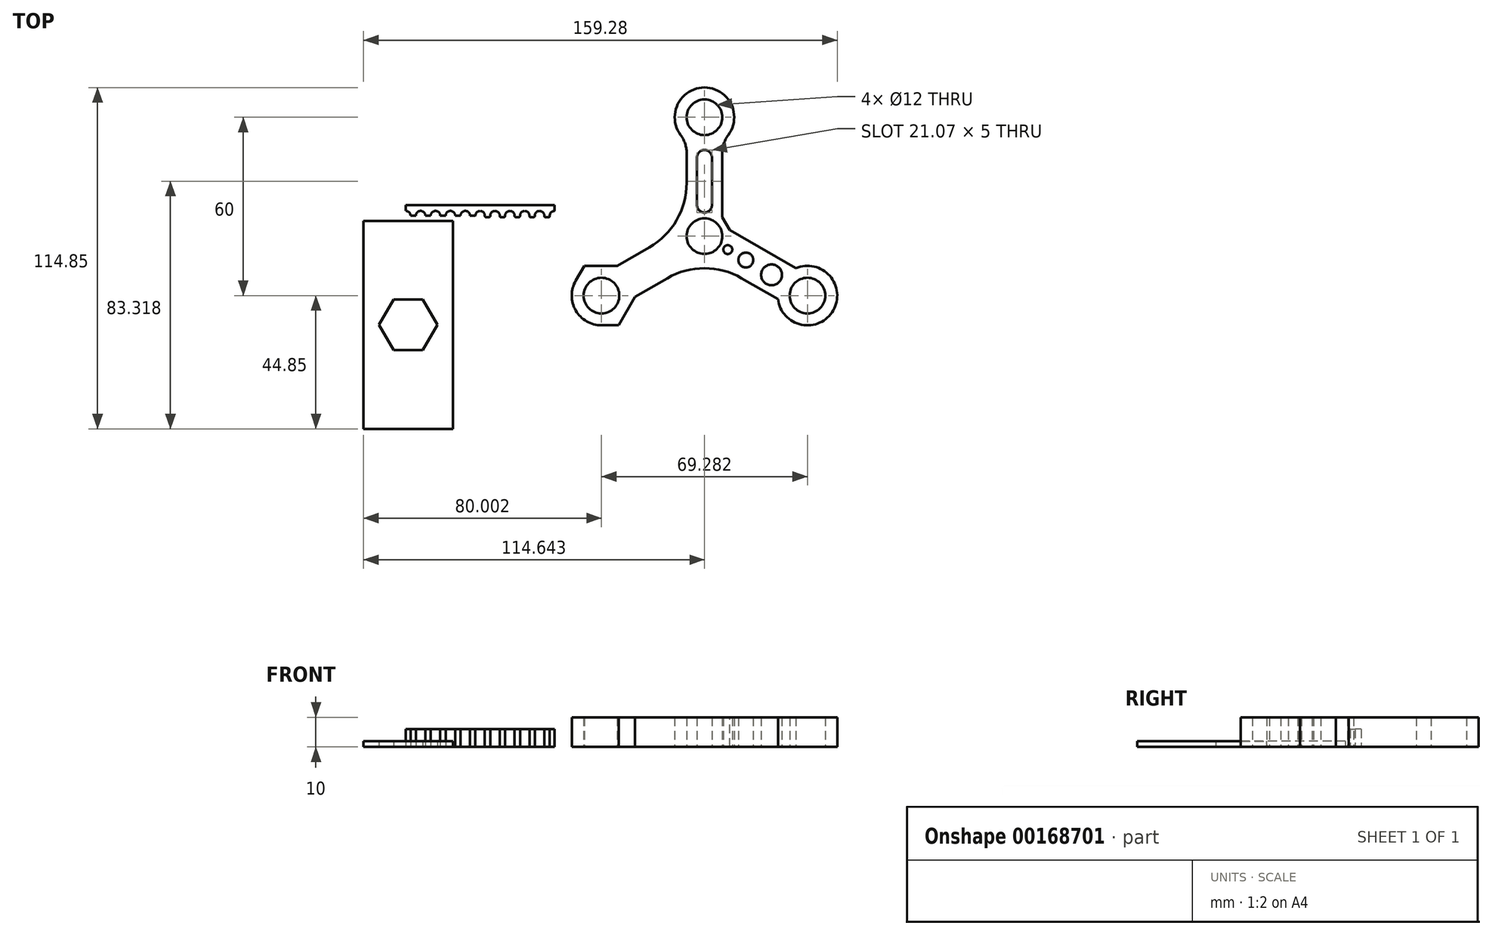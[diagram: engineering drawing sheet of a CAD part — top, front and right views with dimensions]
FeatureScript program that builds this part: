
annotation { "Feature Type Name" : "Feature", "Feature Type Description" : "" }
export const myFeature = defineFeature(function(context is Context, id is Id, definition is map)
    precondition{}
    {
        {
            var Q0;
            Q0=qCreatedBy(makeId("Top.planeOp"),FACE);
            var sketch = newSketch(context, id + "F0", { "sketchPlane" : qUnion([Q0])});
            skLineSegment(sketch, "E0", {"start": v(-55.05, 8.38) * mm, "end": v(-5.05, 8.38) * mm, "construction": true});
            skLineSegment(sketch, "E1.0", {"start": v(-55.05, 6.89) * mm, "end": v(-5.05, 6.89) * mm, "construction": true});
            skLineSegment(sketch, "E2.0", {"start": v(-55.05, 4.58) * mm, "end": v(-5.05, 4.58) * mm});
            skLineSegment(sketch, "E3", {"start": v(-36.36, 4.58) * mm, "end": v(-36.36, 8.38) * mm, "construction": true});
            skArc(sketch, "E4", {"start": v(-37.95, 6.89) * mm, "mid": v(-36.36, 8.48) * mm, "end": v(-34.77, 6.89) * mm});
            skLineSegment(sketch, "E5.0", {"start": v(-55.05, 6.32) * mm, "end": v(-5.05, 6.32) * mm, "construction": true});
            skLineSegment(sketch, "E6", {"start": v(-34.27, 6.32) * mm, "end": v(-32.77, 6.32) * mm});
            skLineSegment(sketch, "E7", {"start": v(-34.77, 6.89) * mm, "end": v(-34.77, 6.82) * mm});
            skLineSegment(sketch, "E8", {"start": v(-37.95, 6.89) * mm, "end": v(-37.95, 6.82) * mm});
            skLineSegment(sketch, "E9", {"start": v(-38.45, 6.32) * mm, "end": v(-38.95, 6.32) * mm});
            skPoint(sketch, "E10.visualSharp", {"position": v(-37.95, 6.32) * mm});
            skArc(sketch, "E10.filletArc", {"start": v(-38.45, 6.32) * mm, "mid": v(-38.1, 6.46) * mm, "end": v(-37.95, 6.82) * mm});
            skPoint(sketch, "E11.visualSharp", {"position": v(-34.77, 6.32) * mm});
            skArc(sketch, "E11.filletArc", {"start": v(-34.77, 6.82) * mm, "mid": v(-34.63, 6.46) * mm, "end": v(-34.27, 6.32) * mm});
            skLineSegment(sketch, "E12.1.0.0", {"start": v(-33.45, 6.32) * mm, "end": v(-33.95, 6.32) * mm});
            skArc(sketch, "E12.1.0.1", {"start": v(-33.45, 6.32) * mm, "mid": v(-33.1, 6.46) * mm, "end": v(-32.95, 6.82) * mm});
            skLineSegment(sketch, "E12.1.0.2", {"start": v(-32.95, 6.89) * mm, "end": v(-32.95, 6.82) * mm});
            skArc(sketch, "E12.1.0.3", {"start": v(-32.95, 6.89) * mm, "mid": v(-31.36, 8.48) * mm, "end": v(-29.77, 6.89) * mm});
            skLineSegment(sketch, "E12.1.0.4", {"start": v(-29.77, 6.89) * mm, "end": v(-29.77, 6.82) * mm});
            skArc(sketch, "E12.1.0.5", {"start": v(-29.77, 6.82) * mm, "mid": v(-29.63, 6.46) * mm, "end": v(-29.27, 6.32) * mm});
            skLineSegment(sketch, "E12.1.0.6", {"start": v(-29.27, 6.32) * mm, "end": v(-27.77, 6.32) * mm});
            skLineSegment(sketch, "E12.2.0.0", {"start": v(-28.45, 6.32) * mm, "end": v(-28.95, 6.32) * mm});
            skArc(sketch, "E12.2.0.1", {"start": v(-28.45, 6.32) * mm, "mid": v(-28.1, 6.46) * mm, "end": v(-27.95, 6.82) * mm});
            skLineSegment(sketch, "E12.2.0.2", {"start": v(-27.95, 6.89) * mm, "end": v(-27.95, 6.82) * mm});
            skArc(sketch, "E12.2.0.3", {"start": v(-27.95, 6.89) * mm, "mid": v(-26.36, 8.48) * mm, "end": v(-24.77, 6.89) * mm});
            skLineSegment(sketch, "E12.2.0.4", {"start": v(-24.77, 6.89) * mm, "end": v(-24.77, 6.82) * mm});
            skArc(sketch, "E12.2.0.5", {"start": v(-24.77, 6.82) * mm, "mid": v(-24.63, 6.46) * mm, "end": v(-24.27, 6.32) * mm});
            skLineSegment(sketch, "E12.2.0.6", {"start": v(-24.27, 6.32) * mm, "end": v(-22.77, 6.32) * mm});
            skLineSegment(sketch, "E12.3.0.0", {"start": v(-23.45, 6.32) * mm, "end": v(-23.95, 6.32) * mm});
            skArc(sketch, "E12.3.0.1", {"start": v(-23.45, 6.32) * mm, "mid": v(-23.1, 6.46) * mm, "end": v(-22.95, 6.82) * mm});
            skLineSegment(sketch, "E12.3.0.2", {"start": v(-22.95, 6.89) * mm, "end": v(-22.95, 6.82) * mm});
            skArc(sketch, "E12.3.0.3", {"start": v(-22.95, 6.89) * mm, "mid": v(-21.36, 8.48) * mm, "end": v(-19.77, 6.89) * mm});
            skLineSegment(sketch, "E12.3.0.4", {"start": v(-19.77, 6.89) * mm, "end": v(-19.77, 6.82) * mm});
            skArc(sketch, "E12.3.0.5", {"start": v(-19.77, 6.82) * mm, "mid": v(-19.63, 6.46) * mm, "end": v(-19.27, 6.32) * mm});
            skLineSegment(sketch, "E12.3.0.6", {"start": v(-19.27, 6.32) * mm, "end": v(-17.77, 6.32) * mm});
            skLineSegment(sketch, "E12.4.0.0", {"start": v(-18.45, 6.32) * mm, "end": v(-18.95, 6.32) * mm});
            skArc(sketch, "E12.4.0.1", {"start": v(-18.45, 6.32) * mm, "mid": v(-18.1, 6.46) * mm, "end": v(-17.95, 6.82) * mm});
            skLineSegment(sketch, "E12.4.0.2", {"start": v(-17.95, 6.89) * mm, "end": v(-17.95, 6.82) * mm});
            skArc(sketch, "E12.4.0.3", {"start": v(-17.95, 6.89) * mm, "mid": v(-16.36, 8.48) * mm, "end": v(-14.77, 6.89) * mm});
            skLineSegment(sketch, "E12.4.0.4", {"start": v(-14.77, 6.89) * mm, "end": v(-14.77, 6.82) * mm});
            skArc(sketch, "E12.4.0.5", {"start": v(-14.77, 6.82) * mm, "mid": v(-14.63, 6.46) * mm, "end": v(-14.27, 6.32) * mm});
            skLineSegment(sketch, "E12.4.0.6", {"start": v(-14.27, 6.32) * mm, "end": v(-12.77, 6.32) * mm});
            skLineSegment(sketch, "E12.direction1", {"start": v(-38.95, 6.32) * mm, "end": v(-33.95, 6.32) * mm, "construction": true});
            skLineSegment(sketch, "E13.0.5.0", {"start": v(-13.45, 6.32) * mm, "end": v(-13.95, 6.32) * mm});
            skArc(sketch, "E13.3.5.0", {"start": v(-13.45, 6.32) * mm, "mid": v(-13.1, 6.46) * mm, "end": v(-12.95, 6.82) * mm});
            skLineSegment(sketch, "E13.7.5.0", {"start": v(-12.95, 6.89) * mm, "end": v(-12.95, 6.82) * mm});
            skArc(sketch, "E13.10.5.0", {"start": v(-12.95, 6.89) * mm, "mid": v(-11.36, 8.48) * mm, "end": v(-9.77, 6.89) * mm});
            skLineSegment(sketch, "E13.14.5.0", {"start": v(-9.77, 6.89) * mm, "end": v(-9.77, 6.82) * mm});
            skArc(sketch, "E13.17.5.0", {"start": v(-9.77, 6.82) * mm, "mid": v(-9.63, 6.46) * mm, "end": v(-9.27, 6.32) * mm});
            skLineSegment(sketch, "E13.21.5.0", {"start": v(-9.27, 6.32) * mm, "end": v(-7.77, 6.32) * mm});
            skLineSegment(sketch, "E14", {"start": v(-36.36, 8.48) * mm, "end": v(-36.36, 10.48) * mm});
            skPoint(sketch, "E14.endSnap0", {"position": v(-36.36, 8.48) * mm});
            skLineSegment(sketch, "E15", {"start": v(-36.36, 10.48) * mm, "end": v(-11.36, 10.48) * mm});
            skLineSegment(sketch, "E16", {"start": v(-11.36, 10.48) * mm, "end": v(-11.36, 8.48) * mm});
            skCircle(sketch, "E17", {"center": v(-41.36, 6.89) * mm, "radius": 1.6 * mm});
            skCircle(sketch, "E18.1.0.0", {"center": v(-46.36, 6.89) * mm, "radius": 1.6 * mm});
            skCircle(sketch, "E18.2.0.0", {"center": v(-51.36, 6.89) * mm, "radius": 1.6 * mm});
            skCircle(sketch, "E18.3.0.0", {"center": v(-56.36, 6.89) * mm, "radius": 1.6 * mm});
            skCircle(sketch, "E18.4.0.0", {"center": v(-61.36, 6.89) * mm, "radius": 1.6 * mm});
            skCircle(sketch, "E18.5.0.0", {"center": v(-66.36, 6.89) * mm, "radius": 1.6 * mm});
            skLineSegment(sketch, "E18.direction1", {"start": v(-41.36, 6.89) * mm, "end": v(-46.36, 6.89) * mm, "construction": true});
            skLineSegment(sketch, "E19", {"start": v(-39.76, 6.89) * mm, "end": v(-37.95, 6.89) * mm});
            skLineSegment(sketch, "E20", {"start": v(-36.36, 10.48) * mm, "end": v(-61.36, 10.48) * mm});
            skLineSegment(sketch, "E21", {"start": v(-61.36, 10.48) * mm, "end": v(-61.36, 8.49) * mm});
            skLineSegment(sketch, "E22", {"start": v(-59.76, 6.89) * mm, "end": v(-57.96, 6.89) * mm});
            skLineSegment(sketch, "E23", {"start": v(-54.76, 6.89) * mm, "end": v(-52.96, 6.89) * mm});
            skLineSegment(sketch, "E24", {"start": v(-49.76, 6.89) * mm, "end": v(-47.96, 6.89) * mm});
            skLineSegment(sketch, "E25", {"start": v(-44.76, 6.89) * mm, "end": v(-42.96, 6.89) * mm});
            skSolve(sketch);
        }
        {
            var Q0;
            {var subQ5=sQuery(id+"F0.wireOp",EDGE,"E14");Q0=makeQuery(id+"F0.imprint","IMPRINT",FACE,{"disambiguationData":[TD([[makeQuery(id+"F0.imprint","IMPRINT",EDGE,{"derivedFrom":subQ5}),1.0]])]});}
            var Q1;
            {var subQ7=sQuery(id+"F0.wireOp",EDGE,"E7");Q1=makeQuery(id+"F0.imprint","IMPRINT",FACE,{"disambiguationData":[TD([[makeQuery(id+"F0.imprint","IMPRINT",EDGE,{"derivedFrom":subQ7}),1.0]])]});}
            extrude(context, id + "F1", {"entities" : qUnion([Q0, Q1]), "depth" : 6 * mm});
        }
        {
            var Q0;
            Q0=qCreatedBy(makeId("Top.planeOp"),FACE);
            var sketch = newSketch(context, id + "F2", { "sketchPlane" : qUnion([Q0])});
            skCircle(sketch, "E26", {"center": v(39.08, 0) * mm, "radius": 6 * mm});
            skLineSegment(sketch, "E27", {"start": v(33.08, 0) * mm, "end": v(45.08, 0) * mm, "construction": true});
            skLineSegment(sketch, "E28.bottom", {"start": v(33.08, 0) * mm, "end": v(45.08, 0) * mm});
            skLineSegment(sketch, "E28.top", {"start": v(33.08, 40) * mm, "end": v(45.08, 40) * mm});
            skLineSegment(sketch, "E28.left", {"start": v(33.08, 0) * mm, "end": v(33.08, 28) * mm});
            skLineSegment(sketch, "E28.right", {"start": v(45.08, 0) * mm, "end": v(45.08, 28) * mm});
            skCircle(sketch, "E29", {"center": v(39.08, 40) * mm, "radius": 6 * mm});
            skLineSegment(sketch, "E30.1.0", {"start": v(36.08, 5.2) * mm, "end": v(1.44, -14.8) * mm});
            skCircle(sketch, "E30.1.1", {"center": v(4.44, -20) * mm, "radius": 10 * mm});
            skCircle(sketch, "E30.1.2", {"center": v(4.44, -20) * mm, "radius": 6 * mm});
            skLineSegment(sketch, "E30.1.3", {"start": v(42.08, -5.2) * mm, "end": v(7.44, -25.2) * mm});
            skLineSegment(sketch, "E30.2.0", {"start": v(36.08, -5.2) * mm, "end": v(70.72, -25.2) * mm});
            skCircle(sketch, "E30.2.1", {"center": v(73.72, -20) * mm, "radius": 10 * mm});
            skCircle(sketch, "E30.2.2", {"center": v(73.72, -20) * mm, "radius": 6 * mm});
            skLineSegment(sketch, "E30.2.3", {"start": v(42.08, 5.2) * mm, "end": v(76.72, -14.8) * mm});
            skLineSegment(sketch, "E31", {"start": v(39.08, 10.43) * mm, "end": v(39.08, 26.5) * mm});
            skArc(sketch, "E32.0.startCap", {"start": v(41.58, 10.43) * mm, "mid": v(39.08, 7.93) * mm, "end": v(36.58, 10.43) * mm});
            skArc(sketch, "E32.0.endCap", {"start": v(36.58, 26.5) * mm, "mid": v(39.08, 29) * mm, "end": v(41.58, 26.5) * mm});
            skLineSegment(sketch, "E32.0.left", {"start": v(36.58, 10.43) * mm, "end": v(36.58, 26.5) * mm});
            skLineSegment(sketch, "E32.0.right", {"start": v(41.58, 10.43) * mm, "end": v(41.58, 26.5) * mm});
            skCircle(sketch, "E33.cCircle", {"center": v(4.44, -20) * mm, "radius": 10 * mm, "construction": true});
            skLineSegment(sketch, "E33.0", {"start": v(-1.33, -10) * mm, "end": v(10.22, -10) * mm});
            skLineSegment(sketch, "E33.1", {"start": v(10.22, -10) * mm, "end": v(15.99, -20) * mm});
            skLineSegment(sketch, "E33.2", {"start": v(15.99, -20) * mm, "end": v(10.22, -30) * mm});
            skLineSegment(sketch, "E33.3", {"start": v(10.22, -30) * mm, "end": v(-1.33, -30) * mm});
            skLineSegment(sketch, "E33.4", {"start": v(-1.33, -30) * mm, "end": v(-7.1, -20) * mm});
            skLineSegment(sketch, "E33.5", {"start": v(-7.1, -20) * mm, "end": v(-1.33, -10) * mm});
            skPoint(sketch, "E33.0.midPoint", {"position": v(4.44, -10) * mm});
            skLineSegment(sketch, "E34.bottom", {"start": v(-75.56, 5.15) * mm, "end": v(-45.56, 5.15) * mm});
            skLineSegment(sketch, "E34.top", {"start": v(-75.56, -64.85) * mm, "end": v(-45.56, -64.85) * mm});
            skLineSegment(sketch, "E34.left", {"start": v(-75.56, 5.15) * mm, "end": v(-75.56, -64.85) * mm});
            skLineSegment(sketch, "E34.right", {"start": v(-45.56, 5.15) * mm, "end": v(-45.56, -64.85) * mm});
            skCircle(sketch, "E35.cCircle", {"center": v(-60.56, -29.85) * mm, "radius": 8.5 * mm, "construction": true});
            skPoint(sketch, "E35.cCircle.centerSnap0", {"position": v(-60.56, -64.85) * mm});
            skPoint(sketch, "E35.cCircle.centerSnap1", {"position": v(-75.56, -29.85) * mm});
            skLineSegment(sketch, "E35.0", {"start": v(-65.46, -21.35) * mm, "end": v(-55.65, -21.35) * mm});
            skLineSegment(sketch, "E35.1", {"start": v(-55.65, -21.35) * mm, "end": v(-50.74, -29.85) * mm});
            skLineSegment(sketch, "E35.2", {"start": v(-50.74, -29.85) * mm, "end": v(-55.65, -38.35) * mm});
            skLineSegment(sketch, "E35.3", {"start": v(-55.65, -38.35) * mm, "end": v(-65.46, -38.35) * mm});
            skLineSegment(sketch, "E35.4", {"start": v(-65.46, -38.35) * mm, "end": v(-70.37, -29.85) * mm});
            skLineSegment(sketch, "E35.5", {"start": v(-70.37, -29.85) * mm, "end": v(-65.46, -21.35) * mm});
            skPoint(sketch, "E35.0.midPoint", {"position": v(-60.56, -21.35) * mm});
            skLineSegment(sketch, "E36", {"start": v(39.08, 0) * mm, "end": v(73.72, -20) * mm, "construction": true});
            skCircle(sketch, "E37", {"center": v(46.93, -4.53) * mm, "radius": 1.5 * mm});
            skCircle(sketch, "E38", {"center": v(53, -8.03) * mm, "radius": 2.5 * mm});
            skCircle(sketch, "E39", {"center": v(61.65, -13.03) * mm, "radius": 3.5 * mm});
            skArc(sketch, "E40", {"start": v(33.08, 32) * mm, "mid": v(39.08, 30) * mm, "end": v(45.08, 32) * mm});
            skArc(sketch, "E41", {"start": v(47.08, 34) * mm, "mid": v(39.08, 50) * mm, "end": v(31.08, 34) * mm});
            skPoint(sketch, "E42.newPointB", {"position": v(33.08, 40) * mm});
            skArc(sketch, "E42.filletArc", {"start": v(33.08, 28) * mm, "mid": v(32.57, 31.16) * mm, "end": v(31.08, 34) * mm});
            skPoint(sketch, "E43.newPointB", {"position": v(45.08, 40) * mm});
            skArc(sketch, "E43.filletArc", {"start": v(47.08, 34) * mm, "mid": v(45.6, 31.16) * mm, "end": v(45.08, 28) * mm});
            skSolve(sketch);
        }
        {
            var Q0;
            {var subQ1=sQuery(id+"F2.wireOp",EDGE,"E28.left");var subQ4=sQuery(id+"F2.wireOp",EDGE,"c7i8PMyH-ycge-szl3-A97O-6cANzthIr7NN");var subQ5=makeQuery(id+"F2.imprint","INTERSECT",VERTEX,{"derivedFrom":[subQ1,subQ4]});Q0=makeQuery(id+"F2.imprint","IMPRINT",FACE,{"disambiguationData":[TD([[makeQuery(id+"F2.imprint","IMPRINT",EDGE,{"disambiguationData":[TD([[subQ5,1.0]])],"derivedFrom":subQ4}),1.0]])]});}
            var Q1;
            {var subQ1=sQuery(id+"F2.wireOp",EDGE,"E28.left");var subQ4=sQuery(id+"F2.wireOp",EDGE,"c7i8PMyH-ycge-szl3-A97O-6cANzthIr7NN");var subQ5=makeQuery(id+"F2.imprint","INTERSECT",VERTEX,{"derivedFrom":[subQ1,subQ4]});Q1=makeQuery(id+"F2.imprint","IMPRINT",FACE,{"disambiguationData":[TD([[makeQuery(id+"F2.imprint","IMPRINT",EDGE,{"disambiguationData":[TD([[subQ5,-1.0]])],"derivedFrom":subQ4}),1.0]])]});}
            var Q2;
            {var subQ5=sQuery(id+"F2.wireOp",EDGE,"E30.1.0");var subQ6=sQuery(id+"F2.wireOp",EDGE,"E26");var subQ7=makeQuery(id+"F2.imprint","INTERSECT",VERTEX,{"derivedFrom":[subQ6,subQ5]});Q2=makeQuery(id+"F2.imprint","IMPRINT",FACE,{"disambiguationData":[TD([[makeQuery(id+"F2.imprint","IMPRINT",EDGE,{"disambiguationData":[TD([[subQ7,1.0]])],"derivedFrom":subQ6}),-1.0]])]});}
            var Q3;
            {var subQ1=sQuery(id+"F2.wireOp",EDGE,"E30.1.0");var subQ5=sQuery(id+"F2.wireOp",EDGE,"E28.left");var subQ6=makeQuery(id+"F2.imprint","INTERSECT",VERTEX,{"derivedFrom":[subQ5,subQ1]});Q3=makeQuery(id+"F2.imprint","IMPRINT",FACE,{"disambiguationData":[TD([[makeQuery(id+"F2.imprint","IMPRINT",EDGE,{"disambiguationData":[TD([[subQ6,-1.0]])],"derivedFrom":subQ1}),1.0]])]});}
            var Q4;
            {var subQ0=sQuery(id+"F2.wireOp",EDGE,"E30.1.2");var subQ1=sQuery(id+"F2.wireOp",EDGE,"E30.1.0");var subQ2=makeQuery(id+"F2.imprint","INTERSECT",VERTEX,{"derivedFrom":[subQ1,subQ0]});Q4=makeQuery(id+"F2.imprint","IMPRINT",FACE,{"disambiguationData":[TD([[makeQuery(id+"F2.imprint","IMPRINT",EDGE,{"disambiguationData":[TD([[subQ2,1.0]])],"derivedFrom":subQ1}),1.0]])]});}
            var Q5;
            {var subQ0=sQuery(id+"F2.wireOp",EDGE,"E30.1.2");var subQ1=sQuery(id+"F2.wireOp",EDGE,"E30.1.0");var subQ2=makeQuery(id+"F2.imprint","INTERSECT",VERTEX,{"derivedFrom":[subQ1,subQ0]});Q5=makeQuery(id+"F2.imprint","IMPRINT",FACE,{"disambiguationData":[TD([[makeQuery(id+"F2.imprint","IMPRINT",EDGE,{"disambiguationData":[TD([[subQ2,1.0]])],"derivedFrom":subQ1}),-1.0]])]});}
            var Q6;
            {var subQ1=sQuery(id+"F2.wireOp",EDGE,"E30.1.3");var subQ6=sQuery(id+"F2.wireOp",EDGE,"E26");var subQ10=makeQuery(id+"F2.imprint","INTERSECT",VERTEX,{"derivedFrom":[subQ6,subQ1]});Q6=makeQuery(id+"F2.imprint","IMPRINT",FACE,{"disambiguationData":[TD([[makeQuery(id+"F2.imprint","IMPRINT",EDGE,{"disambiguationData":[TD([[subQ10,-1.0]])],"derivedFrom":subQ1}),1.0]])]});}
            var Q7;
            {var subQ0=sQuery(id+"F2.wireOp",EDGE,"E30.2.2");var subQ1=sQuery(id+"F2.wireOp",EDGE,"E30.2.0");var subQ2=makeQuery(id+"F2.imprint","INTERSECT",VERTEX,{"derivedFrom":[subQ1,subQ0]});Q7=makeQuery(id+"F2.imprint","IMPRINT",FACE,{"disambiguationData":[TD([[makeQuery(id+"F2.imprint","IMPRINT",EDGE,{"disambiguationData":[TD([[subQ2,1.0]])],"derivedFrom":subQ1}),-1.0]])]});}
            var Q8;
            {var subQ0=sQuery(id+"F2.wireOp",EDGE,"E30.2.2");var subQ1=sQuery(id+"F2.wireOp",EDGE,"E30.2.0");var subQ2=makeQuery(id+"F2.imprint","INTERSECT",VERTEX,{"derivedFrom":[subQ1,subQ0]});Q8=makeQuery(id+"F2.imprint","IMPRINT",FACE,{"disambiguationData":[TD([[makeQuery(id+"F2.imprint","IMPRINT",EDGE,{"disambiguationData":[TD([[subQ2,1.0]])],"derivedFrom":subQ1}),1.0]])]});}
            var Q9;
            {var subQ0=sQuery(id+"F2.wireOp",EDGE,"E30.1.3");var subQ1=sQuery(id+"F2.wireOp",EDGE,"E26");var subQ2=makeQuery(id+"F2.imprint","INTERSECT",VERTEX,{"derivedFrom":[subQ1,subQ0]});Q9=makeQuery(id+"F2.imprint","IMPRINT",FACE,{"disambiguationData":[TD([[makeQuery(id+"F2.imprint","IMPRINT",EDGE,{"disambiguationData":[TD([[subQ2,1.0]])],"derivedFrom":subQ1}),-1.0]])]});}
            var Q10;
            {var subQ1=sQuery(id+"F2.wireOp",EDGE,"E26");var subQ3=sQuery(id+"F2.wireOp",EDGE,"E30.1.0");var subQ4=makeQuery(id+"F2.imprint","INTERSECT",VERTEX,{"derivedFrom":[subQ1,subQ3]});Q10=makeQuery(id+"F2.imprint","IMPRINT",FACE,{"disambiguationData":[TD([[makeQuery(id+"F2.imprint","IMPRINT",EDGE,{"disambiguationData":[TD([[subQ4,-1.0]])],"derivedFrom":subQ3}),1.0]])]});}
            var Q11;
            {var subQ1=sQuery(id+"F2.wireOp",EDGE,"E26");var subQ3=sQuery(id+"F2.wireOp",EDGE,"E30.2.3");var subQ4=makeQuery(id+"F2.imprint","INTERSECT",VERTEX,{"derivedFrom":[subQ1,subQ3]});Q11=makeQuery(id+"F2.imprint","IMPRINT",FACE,{"disambiguationData":[TD([[makeQuery(id+"F2.imprint","IMPRINT",EDGE,{"disambiguationData":[TD([[subQ4,-1.0]])],"derivedFrom":subQ3}),-1.0]])]});}
            var Q12;
            {var subQ0=sQuery(id+"F2.wireOp",EDGE,"E33.0");var subQ1=sQuery(id+"F2.wireOp",EDGE,"E30.1.0");var subQ2=makeQuery(id+"F2.imprint","INTERSECT",VERTEX,{"derivedFrom":[subQ1,subQ0]});Q12=makeQuery(id+"F2.imprint","IMPRINT",FACE,{"disambiguationData":[TD([[makeQuery(id+"F2.imprint","IMPRINT",EDGE,{"disambiguationData":[TD([[subQ2,-1.0]])],"derivedFrom":subQ1}),1.0]])]});}
            var Q13;
            {var subQ0=sQuery(id+"F2.wireOp",EDGE,"E33.0");var subQ1=sQuery(id+"F2.wireOp",EDGE,"E30.1.0");var subQ2=makeQuery(id+"F2.imprint","INTERSECT",VERTEX,{"derivedFrom":[subQ1,subQ0]});Q13=makeQuery(id+"F2.imprint","IMPRINT",FACE,{"disambiguationData":[TD([[makeQuery(id+"F2.imprint","IMPRINT",EDGE,{"disambiguationData":[TD([[subQ2,-1.0]])],"derivedFrom":subQ1}),-1.0]])]});}
            var Q14;
            {var subQ0=sQuery(id+"F2.wireOp",EDGE,"E33.5");var subQ1=sQuery(id+"F2.wireOp",EDGE,"E30.1.1");var subQ2=makeQuery(id+"F2.imprint","INTERSECT",VERTEX,{"derivedFrom":[subQ1,subQ0]});Q14=makeQuery(id+"F2.imprint","IMPRINT",FACE,{"disambiguationData":[TD([[makeQuery(id+"F2.imprint","IMPRINT",EDGE,{"disambiguationData":[TD([[subQ2,1.0]])],"derivedFrom":subQ1}),-1.0]])]});}
            var Q15;
            {var subQ0=sQuery(id+"F2.wireOp",EDGE,"E30.1.3");var subQ1=sQuery(id+"F2.wireOp",EDGE,"E30.1.1");var subQ2=makeQuery(id+"F2.imprint","INTERSECT",VERTEX,{"derivedFrom":[subQ1,subQ0]});Q15=makeQuery(id+"F2.imprint","IMPRINT",FACE,{"disambiguationData":[TD([[makeQuery(id+"F2.imprint","IMPRINT",EDGE,{"disambiguationData":[TD([[subQ2,-1.0]])],"derivedFrom":subQ1}),-1.0]])]});}
            var Q16;
            {var subQ0=sQuery(id+"F2.wireOp",EDGE,"E33.2");var subQ1=sQuery(id+"F2.wireOp",EDGE,"E30.1.1");var subQ2=makeQuery(id+"F2.imprint","INTERSECT",VERTEX,{"derivedFrom":[subQ1,subQ0]});Q16=makeQuery(id+"F2.imprint","IMPRINT",FACE,{"disambiguationData":[TD([[makeQuery(id+"F2.imprint","IMPRINT",EDGE,{"disambiguationData":[TD([[subQ2,-1.0]])],"derivedFrom":subQ1}),-1.0]])]});}
            var Q17;
            {var subQ0=sQuery(id+"F2.wireOp",EDGE,"E33.3");var subQ1=sQuery(id+"F2.wireOp",EDGE,"E30.1.1");var subQ2=makeQuery(id+"F2.imprint","INTERSECT",VERTEX,{"derivedFrom":[subQ1,subQ0]});Q17=makeQuery(id+"F2.imprint","IMPRINT",FACE,{"disambiguationData":[TD([[makeQuery(id+"F2.imprint","IMPRINT",EDGE,{"disambiguationData":[TD([[subQ2,-1.0]])],"derivedFrom":subQ1}),-1.0]])]});}
            extrude(context, id + "F3", {"entities" : qUnion([Q0, Q1, Q2, Q3, Q4, Q5, Q6, Q7, Q8, Q9, Q10, Q11, Q12, Q13, Q14, Q15, Q16, Q17]), "depth" : 10 * mm, "offsetDistance" : 25 * mm});
        }
        {
            var Q0;
            Q0=makeQuery(id+"F3.opExtrude","SWEPT_EDGE",EDGE,{"disambiguationData":[OSD([sQuery(id+"F2.wireOp",EDGE,"E28.left"),sQuery(id+"F2.wireOp",EDGE,"E30.1.0")])]});
            var Q1;
            Q1=makeQuery(id+"F3.opExtrude","SWEPT_EDGE",EDGE,{"disambiguationData":[OSD([sQuery(id+"F2.wireOp",EDGE,"E30.1.3"),sQuery(id+"F2.wireOp",EDGE,"E30.2.0")])]});
            fillet(context, id + "F4", {"entities" : qUnion([Q0, Q1]), "radius" : 25 * mm, "tangentPropagation" : true, "allowEdgeOverflow" : false});
        }
        {
            var Q0;
            Q0=makeQuery(id+"F3.opExtrude","SWEPT_EDGE",EDGE,{"disambiguationData":[OSD([sQuery(id+"F2.wireOp",EDGE,"E28.right"),sQuery(id+"F2.wireOp",EDGE,"E30.2.3")])]});
            chamfer(context, id + "F5", {"entities" : qUnion([Q0]), "width" : 5 * mm, "tangentPropagation" : true});
        }
        {
            var Q0;
            Q0=makeQuery(id+"F2.imprint","IMPRINT",FACE,{"disambiguationData":[TD([[makeQuery(id+"F2.imprint","IMPRINT",EDGE,{"derivedFrom":sQuery(id+"F2.wireOp",EDGE,"E34.bottom")}),-1.0]])]});
            extrude(context, id + "F6", {"entities" : qUnion([Q0]), "depth" : 2 * mm, "offsetDistance" : 25 * mm});
        }
    });
